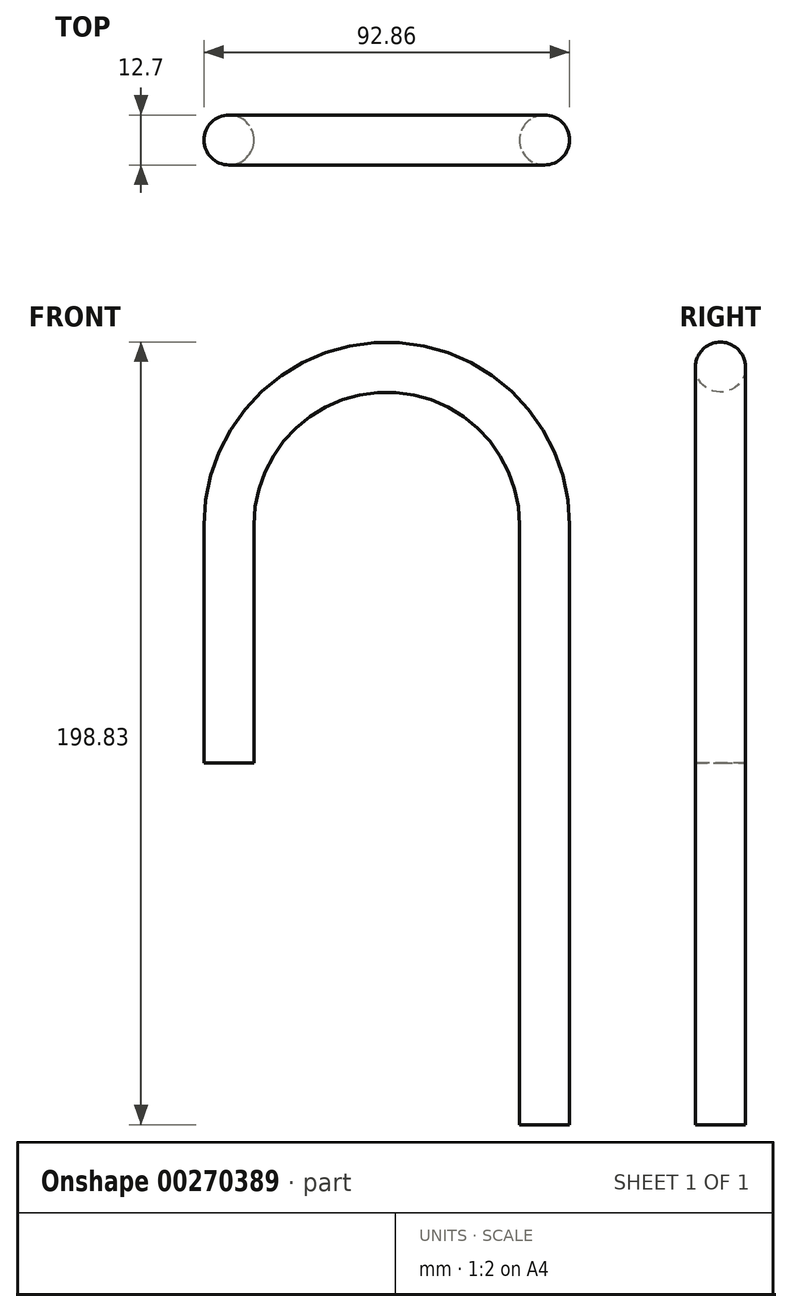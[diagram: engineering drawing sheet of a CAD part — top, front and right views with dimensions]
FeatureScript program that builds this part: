
annotation { "Feature Type Name" : "Feature", "Feature Type Description" : "" }
export const myFeature = defineFeature(function(context is Context, id is Id, definition is map)
    precondition{}
    {
        {
            var Q0;
            Q0=qCreatedBy(makeId("Front.planeOp"),FACE);
            var sketch = newSketch(context, id + "F0", { "sketchPlane" : qUnion([Q0])});
            skLineSegment(sketch, "E0", {"start": v(0, 0) * mm, "end": v(0, 152.4) * mm});
            skArc(sketch, "E1", {"start": v(0, 152.4) * mm, "mid": v(-40.08, 192.48) * mm, "end": v(-80.16, 152.4) * mm});
            skLineSegment(sketch, "E2", {"start": v(-80.16, 152.4) * mm, "end": v(-80.16, 91.85) * mm});
            skSolve(sketch);
        }
        {
            var Q0;
            Q0=qCreatedBy(makeId("Top.planeOp"),FACE);
            var sketch = newSketch(context, id + "F1", { "sketchPlane" : qUnion([Q0])});
            skCircle(sketch, "E3", {"center": v(0, 0) * mm, "radius": 6.35 * mm});
            skSolve(sketch);
        }
        {
            var Q0;
            Q0=makeQuery(id+"F1.imprint","IMPRINT",FACE,{"disambiguationData":[TD([[makeQuery(id+"F1.imprint","IMPRINT",EDGE,{"derivedFrom":sQuery(id+"F1.wireOp",EDGE,"E3")}),1.0]])]});
            var Q1;
            Q1=sQuery(id+"F0.wireOp",EDGE,"E0");
            var Q2;
            Q2=sQuery(id+"F0.wireOp",EDGE,"E1");
            var Q3;
            Q3=sQuery(id+"F0.wireOp",EDGE,"E2");
            sweep(context, id + "F2", {"profiles" : qUnion([Q0]), "path" : qUnion([Q1, Q2, Q3])});
        }
    });
